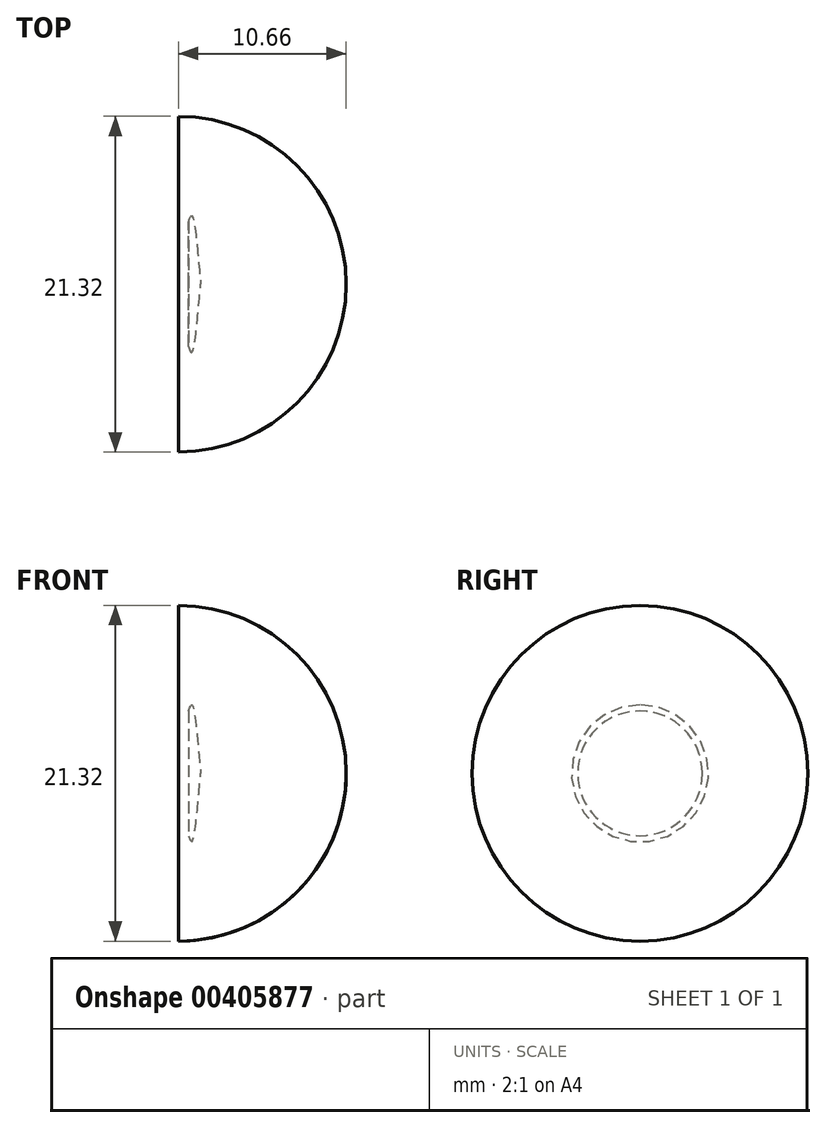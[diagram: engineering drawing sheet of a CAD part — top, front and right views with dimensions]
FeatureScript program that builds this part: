
annotation { "Feature Type Name" : "Feature", "Feature Type Description" : "" }
export const myFeature = defineFeature(function(context is Context, id is Id, definition is map)
    precondition{}
    {
        {
            var Q0;
            Q0=qCreatedBy(makeId("Front.planeOp"),FACE);
            var sketch = newSketch(context, id + "F0", { "sketchPlane" : qUnion([Q0])});
            skArc(sketch, "E0", {"start": v(0, 10.66) * mm, "mid": v(7.54, 7.54) * mm, "end": v(10.66, 0) * mm});
            skLineSegment(sketch, "E1", {"start": v(0, 10.66) * mm, "end": v(0, 0) * mm});
            skLineSegment(sketch, "E2", {"start": v(0.66, 0) * mm, "end": v(0.66, 3.96) * mm});
            skFitSpline(sketch, "E3", {"points": [v(0.66, 3.96) * mm, v(0.84, 4.35) * mm, v(1.42, 0) * mm], "startDerivative": vector(0.77, 2.52) * mm, "endDerivative": vector(0.75, -8.52) * mm});
            skLineSegment(sketch, "E4", {"start": v(0.66, 0) * mm, "end": v(0, 0) * mm});
            skLineSegment(sketch, "E5", {"start": v(1.42, 0) * mm, "end": v(10.66, 0) * mm});
            skSolve(sketch);
        }
        {
            var Q0;
            Q0 = qSketchRegion(id + "F0", true);
            var Q1;
            Q1=sQuery(id+"F0.wireOp",EDGE,"E0");
            var Q2;
            Q2=sQuery(id+"F0.wireOp",EDGE,"E3");
            var Q3;
            Q3=sQuery(id+"F0.wireOp",EDGE,"E1");
            var Q4;
            Q4=sQuery(id+"F0.wireOp",EDGE,"E5");
            var Q5;
            Q5=sQuery(id+"F0.wireOp",EDGE,"E2");
            var Q6;
            Q6=sQuery(id+"F0.wireOp",EDGE,"E4");
            var Q7;
            Q7=sQuery(id+"F0.wireOp",EDGE,"E5");
            revolve(context, id + "F1", {"entities" : qUnion([Q0]), "surfaceEntities" : qUnion([Q1, Q2, Q3, Q4, Q5, Q6]), "axis" : qUnion([Q7]), "revolveType" : RevolveType.FULL});
        }
    });
